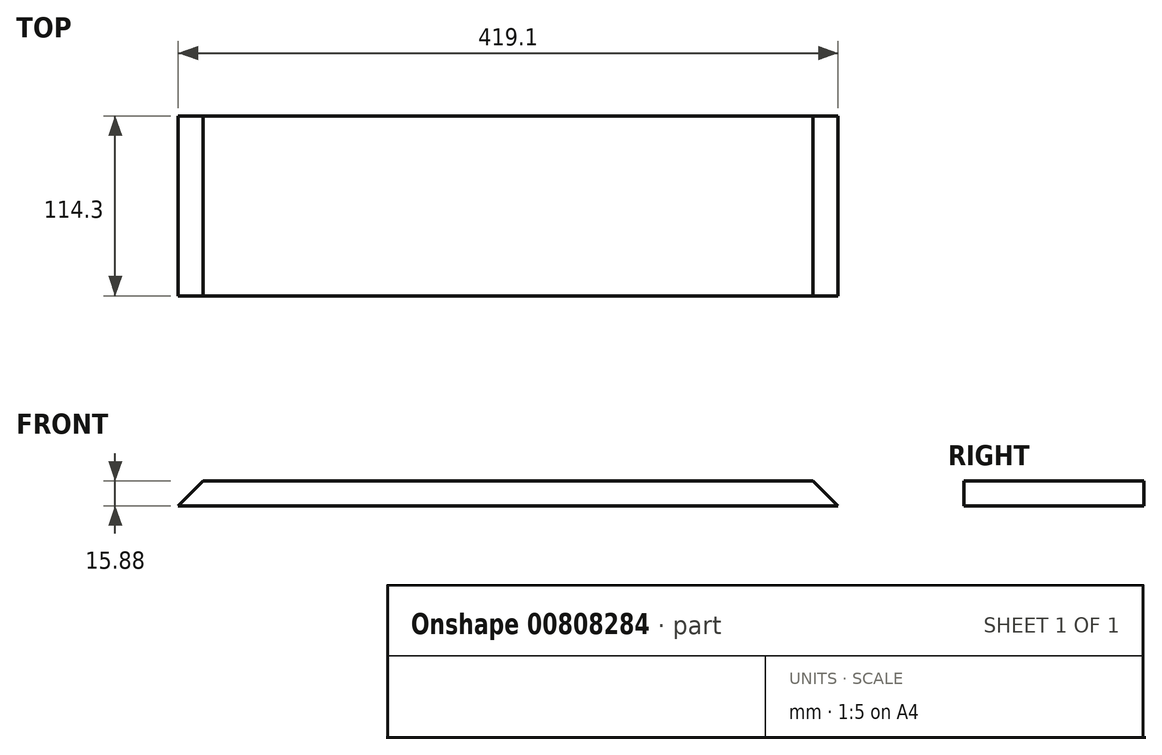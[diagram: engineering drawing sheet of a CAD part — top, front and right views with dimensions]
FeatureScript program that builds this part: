
annotation { "Feature Type Name" : "Feature", "Feature Type Description" : "" }
export const myFeature = defineFeature(function(context is Context, id is Id, definition is map)
    precondition{}
    {
        {
            var Q0;
            Q0=qCreatedBy(makeId("Top.planeOp"),FACE);
            var sketch = newSketch(context, id + "F0", { "sketchPlane" : qUnion([Q0])});
            skLineSegment(sketch, "E0.bottom", {"start": v(209.55, -57.15) * mm, "end": v(-209.55, -57.15) * mm});
            skLineSegment(sketch, "E0.top", {"start": v(209.55, 57.15) * mm, "end": v(-209.55, 57.15) * mm});
            skLineSegment(sketch, "E0.left", {"start": v(209.55, -57.15) * mm, "end": v(209.55, 57.15) * mm});
            skLineSegment(sketch, "E0.right", {"start": v(-209.55, -57.15) * mm, "end": v(-209.55, 57.15) * mm});
            skPoint(sketch, "E0.middle", {"position": v(0, 0) * mm});
            skSolve(sketch);
        }
        {
            var Q0;
            Q0=qSketchRegion(id+"F0",true);
            extrude(context, id + "F1", {"entities" : qUnion([Q0]), "depth" : 15.88 * mm, "offsetDistance" : 25 * mm});
        }
        {
            var Q0;
            Q0=makeQuery(id+"F1.opExtrude","SWEPT_FACE",FACE,{"disambiguationData":[OSD([sQuery(id+"F0.wireOp",EDGE,"E0.bottom")])]});
            var sketch = newSketch(context, id + "F2", { "sketchPlane" : qUnion([Q0])});
            skLineSegment(sketch, "E1", {"start": v(-209.55, 0) * mm, "end": v(-193.68, 15.88) * mm});
            skLineSegment(sketch, "E2", {"start": v(-193.68, 15.88) * mm, "end": v(-193.68, 49.05) * mm});
            skLineSegment(sketch, "E3", {"start": v(-193.68, 49.05) * mm, "end": v(-226.02, 49.05) * mm});
            skLineSegment(sketch, "E4", {"start": v(-226.02, 49.05) * mm, "end": v(-226.02, 0) * mm});
            skLineSegment(sketch, "E5", {"start": v(-226.02, 0) * mm, "end": v(-209.55, 0) * mm});
            skLineSegment(sketch, "E6.0", {"start": v(209.55, 15.88) * mm, "end": v(-209.55, 15.88) * mm, "construction": true});
            skLineSegment(sketch, "E7", {"start": v(0, 15.88) * mm, "end": v(0, 70.31) * mm, "construction": true});
            skLineSegment(sketch, "E8.MirrorCS", {"start": v(193.68, 49.05) * mm, "end": v(226.02, 49.05) * mm});
            skLineSegment(sketch, "E9.MirrorCS", {"start": v(226.02, 0) * mm, "end": v(209.55, 0) * mm});
            skLineSegment(sketch, "E10.MirrorCS", {"start": v(226.02, 49.05) * mm, "end": v(226.02, 0) * mm});
            skLineSegment(sketch, "E11.MirrorCS", {"start": v(209.55, 0) * mm, "end": v(193.68, 15.88) * mm});
            skLineSegment(sketch, "E12.MirrorCS", {"start": v(193.68, 15.88) * mm, "end": v(193.68, 49.05) * mm});
            skSolve(sketch);
        }
        {
            var Q0;
            Q0 = qSketchRegion(id + "F2", true);
            extrude(context, id + "F3", {"entities" : qUnion([Q0]), "operationType" : NewBodyOperationType.REMOVE, "endBound" : BoundingType.THROUGH_ALL, "oppositeDirection" : true, "depth" : 25.4 * mm, "offsetDistance" : 25.4 * mm});
        }
    });
